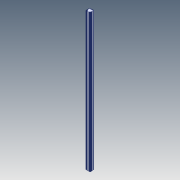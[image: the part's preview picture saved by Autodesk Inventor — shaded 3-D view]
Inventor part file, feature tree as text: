
AUTODESK INVENTOR PART (.ipt)
format: ipt  version: 2020 (Build 240168000, 168)  size: 361,472 bytes
history: native  units: mm
features: other x4, projected_geometry x3, extrude x2, sketch x2
ambient origin geometry x8: Origin, YZ Plane, XZ Plane, XY Plane, X Axis, Y Axis, Z Axis, Center Point
bodies: Body1 (feature_tree), Body2 (feature_tree)
feature tree (11):
  other  "ソリッド1"
  extrude  "押し出し1"  Depth=1300.0mm TaperAngle=0.0deg
  extrude  "押し出し2"  Depth=672.0mm TaperAngle=0.0deg
  other  "ソリッド2"
  sketch  "スケッチ1"
  projected_geometry  "投影ループ1"
  projected_geometry  "投影ループ2"
  sketch  "スケッチ2"
  projected_geometry  "投影ループ3"
  other  "Boss-Extrude1[1]"
  other  "Boss-Extrude1[2]"
